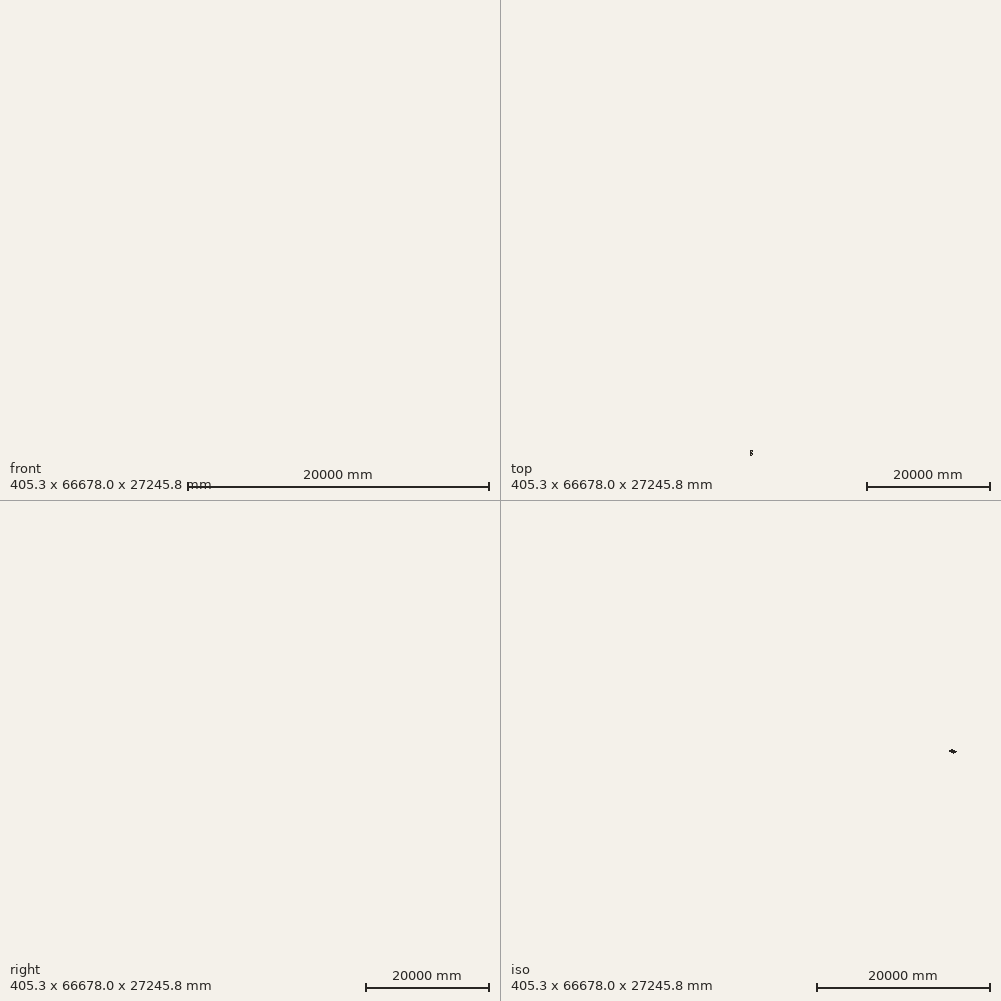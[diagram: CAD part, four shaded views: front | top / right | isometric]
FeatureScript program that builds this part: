
annotation { "Feature Type Name" : "Feature", "Feature Type Description" : "" }
export const myFeature = defineFeature(function(context is Context, id is Id, definition is map)
    precondition{}
    {
        {
            var Q0;
            Q0=qCreatedBy(makeId("Top.planeOp"),FACE);
            var sketch = newSketch(context, id + "F0", { "sketchPlane" : qUnion([Q0])});
            skLineSegment(sketch, "E0", {"start": v(-174.6, -35.65) * mm, "end": v(-124.28, -35.65) * mm});
            skLineSegment(sketch, "E1", {"start": v(-124.28, -35.65) * mm, "end": v(-124.28, -289.85) * mm});
            skLineSegment(sketch, "E2", {"start": v(-124.28, -289.85) * mm, "end": v(-72.03, -289.85) * mm});
            skLineSegment(sketch, "E3", {"start": v(-72.03, -289.85) * mm, "end": v(-72.03, -35.65) * mm});
            skLineSegment(sketch, "E4", {"start": v(-72.03, -35.65) * mm, "end": v(5.25, -35.65) * mm});
            skLineSegment(sketch, "E5", {"start": v(5.25, -35.65) * mm, "end": v(0, -289.85) * mm});
            skLineSegment(sketch, "E6", {"start": v(0, -289.85) * mm, "end": v(50.55, -290.9) * mm});
            skLineSegment(sketch, "E7", {"start": v(50.55, -290.9) * mm, "end": v(50.55, -35.65) * mm});
            skLineSegment(sketch, "E8", {"start": v(50.55, -35.65) * mm, "end": v(126.92, -35.65) * mm});
            skLineSegment(sketch, "E9", {"start": v(126.92, -35.65) * mm, "end": v(126.92, -289.85) * mm});
            skLineSegment(sketch, "E10", {"start": v(126.92, -289.85) * mm, "end": v(179.8, -289.85) * mm});
            skLineSegment(sketch, "E11", {"start": v(179.8, -289.85) * mm, "end": v(179.8, 322.53) * mm});
            skLineSegment(sketch, "E12", {"start": v(179.8, 322.53) * mm, "end": v(126.92, 322.53) * mm});
            skLineSegment(sketch, "E13", {"start": v(126.92, 322.53) * mm, "end": v(126.92, 63.9) * mm});
            skLineSegment(sketch, "E14", {"start": v(126.92, 63.9) * mm, "end": v(50.55, 63.9) * mm});
            skLineSegment(sketch, "E15", {"start": v(50.55, 63.9) * mm, "end": v(50.55, 322.53) * mm});
            skLineSegment(sketch, "E16", {"start": v(50.55, 322.53) * mm, "end": v(5.25, 323.47) * mm});
            skLineSegment(sketch, "E17", {"start": v(5.25, 323.47) * mm, "end": v(5.25, 63.9) * mm});
            skLineSegment(sketch, "E18", {"start": v(5.25, 63.9) * mm, "end": v(-72.03, 65.5) * mm});
            skLineSegment(sketch, "E19", {"start": v(-72.03, 65.5) * mm, "end": v(-72.03, 322.53) * mm});
            skLineSegment(sketch, "E20", {"start": v(-72.03, 322.53) * mm, "end": v(-124.28, 322.53) * mm});
            skLineSegment(sketch, "E21", {"start": v(-124.28, 322.53) * mm, "end": v(-124.28, 63.9) * mm});
            skLineSegment(sketch, "E22", {"start": v(-124.28, 63.9) * mm, "end": v(-174.6, 63.9) * mm});
            skLineSegment(sketch, "E23", {"start": v(-174.6, 63.9) * mm, "end": v(-174.6, 394) * mm});
            skLineSegment(sketch, "E24", {"start": v(-174.6, 394) * mm, "end": v(230.74, 394) * mm});
            skLineSegment(sketch, "E25", {"start": v(230.74, 394) * mm, "end": v(230.74, -369.8) * mm});
            skLineSegment(sketch, "E26", {"start": v(230.74, -369.8) * mm, "end": v(-174.6, -369.8) * mm});
            skLineSegment(sketch, "E27", {"start": v(-174.6, -369.8) * mm, "end": v(-174.6, -35.65) * mm});
            skSolve(sketch);
        }
        {
            var Q0;
            Q0 = qSketchRegion(id + "F0", true);
            extrude(context, id + "F1", {"entities" : qUnion([Q0]), "depth" : 25.4 * mm, "offsetDistance" : 25.4 * mm});
        }
        {
            var Q0;
            Q0=makeQuery(id+"F1.opExtrude","CAP_FACE",FACE,{"disambiguationData":[OSD([sQuery(id+"F0.wireOp",EDGE,"E0"),sQuery(id+"F0.wireOp",EDGE,"E1"),sQuery(id+"F0.wireOp",EDGE,"E2"),sQuery(id+"F0.wireOp",EDGE,"E3"),sQuery(id+"F0.wireOp",EDGE,"E4"),sQuery(id+"F0.wireOp",EDGE,"E5"),sQuery(id+"F0.wireOp",EDGE,"E6"),sQuery(id+"F0.wireOp",EDGE,"E7"),sQuery(id+"F0.wireOp",EDGE,"E8"),sQuery(id+"F0.wireOp",EDGE,"E9"),sQuery(id+"F0.wireOp",EDGE,"E10"),sQuery(id+"F0.wireOp",EDGE,"E11"),sQuery(id+"F0.wireOp",EDGE,"E12"),sQuery(id+"F0.wireOp",EDGE,"E13"),sQuery(id+"F0.wireOp",EDGE,"E14"),sQuery(id+"F0.wireOp",EDGE,"E15"),sQuery(id+"F0.wireOp",EDGE,"E16"),sQuery(id+"F0.wireOp",EDGE,"E17"),sQuery(id+"F0.wireOp",EDGE,"E18"),sQuery(id+"F0.wireOp",EDGE,"E19"),sQuery(id+"F0.wireOp",EDGE,"E20"),sQuery(id+"F0.wireOp",EDGE,"E21"),sQuery(id+"F0.wireOp",EDGE,"E22"),sQuery(id+"F0.wireOp",EDGE,"E23"),sQuery(id+"F0.wireOp",EDGE,"E24"),sQuery(id+"F0.wireOp",EDGE,"E25"),sQuery(id+"F0.wireOp",EDGE,"E26"),sQuery(id+"F0.wireOp",EDGE,"E27")])],"isStart":false});
            shell(context, id + "F2", {"entities" : qUnion([Q0]), "thickness" : 2.54 * mm});
        }
        {
            var Q0;
            Q0=makeQuery(id+"F2.opShell","OFFSET_FACE",FACE,{"disambiguationData":[OSD([sQuery(id+"F0.wireOp",EDGE,"E0"),sQuery(id+"F0.wireOp",EDGE,"E1"),sQuery(id+"F0.wireOp",EDGE,"E2"),sQuery(id+"F0.wireOp",EDGE,"E3"),sQuery(id+"F0.wireOp",EDGE,"E4"),sQuery(id+"F0.wireOp",EDGE,"E5"),sQuery(id+"F0.wireOp",EDGE,"E6"),sQuery(id+"F0.wireOp",EDGE,"E7"),sQuery(id+"F0.wireOp",EDGE,"E8"),sQuery(id+"F0.wireOp",EDGE,"E9"),sQuery(id+"F0.wireOp",EDGE,"E10"),sQuery(id+"F0.wireOp",EDGE,"E11"),sQuery(id+"F0.wireOp",EDGE,"E12"),sQuery(id+"F0.wireOp",EDGE,"E13"),sQuery(id+"F0.wireOp",EDGE,"E14"),sQuery(id+"F0.wireOp",EDGE,"E15"),sQuery(id+"F0.wireOp",EDGE,"E16"),sQuery(id+"F0.wireOp",EDGE,"E17"),sQuery(id+"F0.wireOp",EDGE,"E18"),sQuery(id+"F0.wireOp",EDGE,"E19"),sQuery(id+"F0.wireOp",EDGE,"E20"),sQuery(id+"F0.wireOp",EDGE,"E21"),sQuery(id+"F0.wireOp",EDGE,"E22"),sQuery(id+"F0.wireOp",EDGE,"E23"),sQuery(id+"F0.wireOp",EDGE,"E24"),sQuery(id+"F0.wireOp",EDGE,"E25"),sQuery(id+"F0.wireOp",EDGE,"E26"),sQuery(id+"F0.wireOp",EDGE,"E27")])]});
            var sketch = newSketch(context, id + "F3", { "sketchPlane" : qUnion([Q0])});
            skLineSegment(sketch, "E28.bottom", {"start": v(-172.06, 391.47) * mm, "end": v(-162.53, 391.47) * mm});
            skLineSegment(sketch, "E28.top", {"start": v(-172.06, 381.16) * mm, "end": v(-162.53, 381.16) * mm});
            skLineSegment(sketch, "E28.left", {"start": v(-172.06, 391.47) * mm, "end": v(-172.06, 381.16) * mm});
            skLineSegment(sketch, "E28.right", {"start": v(-162.53, 391.47) * mm, "end": v(-162.53, 381.16) * mm});
            skLineSegment(sketch, "E29.bottom", {"start": v(-172.06, -367.27) * mm, "end": v(-162.53, -367.27) * mm});
            skLineSegment(sketch, "E29.top", {"start": v(-172.06, -358.02) * mm, "end": v(-162.53, -358.02) * mm});
            skLineSegment(sketch, "E29.left", {"start": v(-172.06, -367.27) * mm, "end": v(-172.06, -358.02) * mm});
            skLineSegment(sketch, "E29.right", {"start": v(-162.53, -367.27) * mm, "end": v(-162.53, -358.02) * mm});
            skLineSegment(sketch, "E30.bottom", {"start": v(228.2, -367.27) * mm, "end": v(218.16, -367.27) * mm});
            skLineSegment(sketch, "E30.top", {"start": v(228.2, -358.02) * mm, "end": v(218.16, -358.02) * mm});
            skLineSegment(sketch, "E30.left", {"start": v(228.2, -367.27) * mm, "end": v(228.2, -358.02) * mm});
            skLineSegment(sketch, "E30.right", {"start": v(218.16, -367.27) * mm, "end": v(218.16, -358.02) * mm});
            skSolve(sketch);
        }
        {
            var Q0;
            Q0 = qSketchRegion(id + "F3", true);
            extrude(context, id + "F4", {"entities" : qUnion([Q0]), "operationType" : NewBodyOperationType.ADD, "depth" : 96.52 * mm, "offsetDistance" : 25.4 * mm});
        }
        {
            var Q0;
            Q0=makeQuery(id+"F2.opShell","OFFSET_FACE",FACE,{"disambiguationData":[OSD([sQuery(id+"F0.wireOp",EDGE,"E0"),sQuery(id+"F0.wireOp",EDGE,"E1"),sQuery(id+"F0.wireOp",EDGE,"E2"),sQuery(id+"F0.wireOp",EDGE,"E3"),sQuery(id+"F0.wireOp",EDGE,"E4"),sQuery(id+"F0.wireOp",EDGE,"E5"),sQuery(id+"F0.wireOp",EDGE,"E6"),sQuery(id+"F0.wireOp",EDGE,"E7"),sQuery(id+"F0.wireOp",EDGE,"E8"),sQuery(id+"F0.wireOp",EDGE,"E9"),sQuery(id+"F0.wireOp",EDGE,"E10"),sQuery(id+"F0.wireOp",EDGE,"E11"),sQuery(id+"F0.wireOp",EDGE,"E12"),sQuery(id+"F0.wireOp",EDGE,"E13"),sQuery(id+"F0.wireOp",EDGE,"E14"),sQuery(id+"F0.wireOp",EDGE,"E15"),sQuery(id+"F0.wireOp",EDGE,"E16"),sQuery(id+"F0.wireOp",EDGE,"E17"),sQuery(id+"F0.wireOp",EDGE,"E18"),sQuery(id+"F0.wireOp",EDGE,"E19"),sQuery(id+"F0.wireOp",EDGE,"E20"),sQuery(id+"F0.wireOp",EDGE,"E21"),sQuery(id+"F0.wireOp",EDGE,"E22"),sQuery(id+"F0.wireOp",EDGE,"E23"),sQuery(id+"F0.wireOp",EDGE,"E24"),sQuery(id+"F0.wireOp",EDGE,"E25"),sQuery(id+"F0.wireOp",EDGE,"E26"),sQuery(id+"F0.wireOp",EDGE,"E27")])]});
            var sketch = newSketch(context, id + "F5", { "sketchPlane" : qUnion([Q0])});
            skLineSegment(sketch, "E31.bottom", {"start": v(-172.06, 66.44) * mm, "end": v(-162.53, 66.44) * mm});
            skLineSegment(sketch, "E31.top", {"start": v(-172.06, 76.58) * mm, "end": v(-162.53, 76.58) * mm});
            skLineSegment(sketch, "E31.left", {"start": v(-172.06, 66.44) * mm, "end": v(-172.06, 76.58) * mm});
            skLineSegment(sketch, "E31.right", {"start": v(-162.53, 66.44) * mm, "end": v(-162.53, 76.58) * mm});
            skLineSegment(sketch, "E32.bottom", {"start": v(-172.06, -38.19) * mm, "end": v(-162.53, -38.19) * mm});
            skLineSegment(sketch, "E32.top", {"start": v(-172.06, -47.6) * mm, "end": v(-162.53, -47.6) * mm});
            skLineSegment(sketch, "E32.left", {"start": v(-172.06, -38.19) * mm, "end": v(-172.06, -47.6) * mm});
            skLineSegment(sketch, "E32.right", {"start": v(-162.53, -38.19) * mm, "end": v(-162.53, -47.6) * mm});
            skSolve(sketch);
        }
        {
            var Q0;
            Q0 = qSketchRegion(id + "F5", true);
            extrude(context, id + "F6", {"entities" : qUnion([Q0]), "operationType" : NewBodyOperationType.ADD, "depth" : 193.04 * mm, "offsetDistance" : 25.4 * mm});
        }
        {
            var Q0;
            Q0=qCreatedBy(makeId("Front.planeOp"),FACE);
            var sketch = newSketch(context, id + "F7", { "sketchPlane" : qUnion([Q0])});
            skLineSegment(sketch, "E33.bottom", {"start": v(-172.06, 195.59) * mm, "end": v(-162.5, 195.59) * mm});
            skLineSegment(sketch, "E33.top", {"start": v(-172.06, 204.26) * mm, "end": v(-162.5, 204.26) * mm});
            skLineSegment(sketch, "E33.left", {"start": v(-172.06, 195.59) * mm, "end": v(-172.06, 204.26) * mm});
            skLineSegment(sketch, "E33.right", {"start": v(-162.5, 195.59) * mm, "end": v(-162.5, 204.26) * mm});
            skSolve(sketch);
        }
        {
            var Q0;
            Q0=makeQuery(id+"F1.opExtrude","SWEPT_BODY",BODY,{"disambiguationData":[OSD([sQuery(id+"F0.wireOp",EDGE,"E0"),sQuery(id+"F0.wireOp",EDGE,"E1"),sQuery(id+"F0.wireOp",EDGE,"E2"),sQuery(id+"F0.wireOp",EDGE,"E3"),sQuery(id+"F0.wireOp",EDGE,"E4"),sQuery(id+"F0.wireOp",EDGE,"E5"),sQuery(id+"F0.wireOp",EDGE,"E6"),sQuery(id+"F0.wireOp",EDGE,"E7"),sQuery(id+"F0.wireOp",EDGE,"E8"),sQuery(id+"F0.wireOp",EDGE,"E9"),sQuery(id+"F0.wireOp",EDGE,"E10"),sQuery(id+"F0.wireOp",EDGE,"E11"),sQuery(id+"F0.wireOp",EDGE,"E12"),sQuery(id+"F0.wireOp",EDGE,"E13"),sQuery(id+"F0.wireOp",EDGE,"E14"),sQuery(id+"F0.wireOp",EDGE,"E15"),sQuery(id+"F0.wireOp",EDGE,"E16"),sQuery(id+"F0.wireOp",EDGE,"E17"),sQuery(id+"F0.wireOp",EDGE,"E18"),sQuery(id+"F0.wireOp",EDGE,"E19"),sQuery(id+"F0.wireOp",EDGE,"E20"),sQuery(id+"F0.wireOp",EDGE,"E21"),sQuery(id+"F0.wireOp",EDGE,"E22"),sQuery(id+"F0.wireOp",EDGE,"E23"),sQuery(id+"F0.wireOp",EDGE,"E24"),sQuery(id+"F0.wireOp",EDGE,"E25"),sQuery(id+"F0.wireOp",EDGE,"E26"),sQuery(id+"F0.wireOp",EDGE,"E27")])]});
            var Q1;
            Q1=qCreatedBy(makeId("Front.planeOp"),FACE);
            transform(context, id + "F8", {"entities" : qUnion([Q0]), "transformType" : TransformType.TRANSLATION_DISTANCE, "transformDirection" : qUnion([Q1]), "distance" : 13.72 * mm, "makeCopy" : false});
        }
        {
            var Q0;
            Q0=makeQuery(id+"F7.imprint","IMPRINT",FACE,{"disambiguationData":[TD([[makeQuery(id+"F7.imprint","IMPRINT",EDGE,{"derivedFrom":sQuery(id+"F7.wireOp",EDGE,"E33.bottom")}),1.0]])]});
            extrude(context, id + "F9", {"entities" : qUnion([Q0]), "endBound" : BoundingType.SYMMETRIC, "depth" : 170.7 * mm, "offsetDistance" : 25.4 * mm});
        }
        {
            var Q0;
            Q0=makeQuery(id+"F9.opExtrude","CAP_EDGE",EDGE,{"disambiguationData":[OSD([sQuery(id+"F7.wireOp",EDGE,"E33.bottom")])],"isStart":true});
            var Q1;
            Q1=makeQuery(id+"F9.opExtrude","CAP_EDGE",EDGE,{"disambiguationData":[OSD([sQuery(id+"F7.wireOp",EDGE,"E33.bottom")])],"isStart":false});
            chamfer(context, id + "F10", {"entities" : qUnion([Q0, Q1]), "width" : 5.08 * mm, "tangentPropagation" : true});
        }
        {
            var Q0;
            Q0=makeQuery(id+"F2.opShell","OFFSET_FACE",FACE,{"disambiguationData":[OSD([sQuery(id+"F0.wireOp",EDGE,"E0"),sQuery(id+"F0.wireOp",EDGE,"E1"),sQuery(id+"F0.wireOp",EDGE,"E2"),sQuery(id+"F0.wireOp",EDGE,"E3"),sQuery(id+"F0.wireOp",EDGE,"E4"),sQuery(id+"F0.wireOp",EDGE,"E5"),sQuery(id+"F0.wireOp",EDGE,"E6"),sQuery(id+"F0.wireOp",EDGE,"E7"),sQuery(id+"F0.wireOp",EDGE,"E8"),sQuery(id+"F0.wireOp",EDGE,"E9"),sQuery(id+"F0.wireOp",EDGE,"E10"),sQuery(id+"F0.wireOp",EDGE,"E11"),sQuery(id+"F0.wireOp",EDGE,"E12"),sQuery(id+"F0.wireOp",EDGE,"E13"),sQuery(id+"F0.wireOp",EDGE,"E14"),sQuery(id+"F0.wireOp",EDGE,"E15"),sQuery(id+"F0.wireOp",EDGE,"E16"),sQuery(id+"F0.wireOp",EDGE,"E17"),sQuery(id+"F0.wireOp",EDGE,"E18"),sQuery(id+"F0.wireOp",EDGE,"E19"),sQuery(id+"F0.wireOp",EDGE,"E20"),sQuery(id+"F0.wireOp",EDGE,"E21"),sQuery(id+"F0.wireOp",EDGE,"E22"),sQuery(id+"F0.wireOp",EDGE,"E23"),sQuery(id+"F0.wireOp",EDGE,"E24"),sQuery(id+"F0.wireOp",EDGE,"E25"),sQuery(id+"F0.wireOp",EDGE,"E26"),sQuery(id+"F0.wireOp",EDGE,"E27")])]});
            var sketch = newSketch(context, id + "F11", { "sketchPlane" : qUnion([Q0])});
            skLineSegment(sketch, "E34.bottom", {"start": v(228.2, 377.75) * mm, "end": v(218.12, 377.75) * mm});
            skLineSegment(sketch, "E34.top", {"start": v(228.2, 367.35) * mm, "end": v(218.12, 367.35) * mm});
            skLineSegment(sketch, "E34.left", {"start": v(228.2, 377.75) * mm, "end": v(228.2, 367.35) * mm});
            skLineSegment(sketch, "E34.right", {"start": v(218.12, 377.75) * mm, "end": v(218.12, 367.35) * mm});
            skSolve(sketch);
        }
        {
            var Q0;
            Q0 = qSketchRegion(id + "F11", true);
            extrude(context, id + "F12", {"entities" : qUnion([Q0]), "operationType" : NewBodyOperationType.ADD, "depth" : 22.86 * mm, "offsetDistance" : 25.4 * mm});
        }
        {
            var Q0;
            Q0=makeQuery(id+"F4.opExtrude","SWEPT_FACE",FACE,{"disambiguationData":[OSD([sQuery(id+"F3.wireOp",EDGE,"E29.left")])]});
            var sketch = newSketch(context, id + "F13", { "sketchPlane" : qUnion([Q0])});
            skLineSegment(sketch, "E35.bottom", {"start": v(380.99, 99.06) * mm, "end": v(382.68, 99.06) * mm});
            skLineSegment(sketch, "E35.top", {"start": v(380.99, 91.4) * mm, "end": v(382.68, 91.4) * mm});
            skLineSegment(sketch, "E35.left", {"start": v(380.99, 99.06) * mm, "end": v(380.99, 91.4) * mm});
            skLineSegment(sketch, "E35.right", {"start": v(382.68, 99.06) * mm, "end": v(382.68, 91.4) * mm});
            skSolve(sketch);
        }
        {
            var Q0;
            Q0 = qSketchRegion(id + "F13", true);
            extrude(context, id + "F14", {"entities" : qUnion([Q0]), "operationType" : NewBodyOperationType.ADD, "oppositeDirection" : true, "depth" : 401.83 * mm, "offsetDistance" : 25.4 * mm});
        }
        {
            var Q0;
            Q0=makeQuery(id+"F14.opExtrude","SWEPT_FACE",FACE,{"disambiguationData":[OSD([sQuery(id+"F13.wireOp",EDGE,"E35.right")])]});
            var sketch = newSketch(context, id + "F15", { "sketchPlane" : qUnion([Q0])});
            skLineSegment(sketch, "E36.bottom", {"start": v(-172.06, 99.06) * mm, "end": v(-173.53, 99.06) * mm});
            skLineSegment(sketch, "E36.top", {"start": v(-172.06, 91.4) * mm, "end": v(-173.53, 91.4) * mm});
            skLineSegment(sketch, "E36.left", {"start": v(-172.06, 99.06) * mm, "end": v(-172.06, 91.4) * mm});
            skLineSegment(sketch, "E36.right", {"start": v(-173.53, 99.06) * mm, "end": v(-173.53, 91.4) * mm});
            skSolve(sketch);
        }
        {
            var Q0;
            Q0 = qSketchRegion(id + "F15", true);
            extrude(context, id + "F16", {"entities" : qUnion([Q0]), "operationType" : NewBodyOperationType.ADD, "oppositeDirection" : true, "depth" : 330.76 * mm, "offsetDistance" : 25.4 * mm});
        }
        {
            var Q0;
            Q0=makeQuery(id+"F6.opExtrude","SWEPT_FACE",FACE,{"disambiguationData":[OSD([sQuery(id+"F5.wireOp",EDGE,"E31.bottom")])]});
            var sketch = newSketch(context, id + "F17", { "sketchPlane" : qUnion([Q0])});
            skLineSegment(sketch, "E37.bottom", {"start": v(-172.06, 99.07) * mm, "end": v(-173.62, 99.07) * mm});
            skLineSegment(sketch, "E37.top", {"start": v(-172.06, 91.41) * mm, "end": v(-173.62, 91.41) * mm});
            skLineSegment(sketch, "E37.left", {"start": v(-172.06, 99.07) * mm, "end": v(-172.06, 91.41) * mm});
            skLineSegment(sketch, "E37.right", {"start": v(-173.62, 99.07) * mm, "end": v(-173.62, 91.41) * mm});
            skSolve(sketch);
        }
        {
            var Q0;
            Q0 = qSketchRegion(id + "F17", true);
            extrude(context, id + "F18", {"entities" : qUnion([Q0]), "operationType" : NewBodyOperationType.ADD, "oppositeDirection" : true, "depth" : 324.87 * mm, "offsetDistance" : 25.4 * mm});
        }
        {
            var Q0;
            Q0=makeQuery(id+"F2.opShell","OFFSET_FACE",FACE,{"disambiguationData":[OSD([sQuery(id+"F0.wireOp",EDGE,"E0"),sQuery(id+"F0.wireOp",EDGE,"E1"),sQuery(id+"F0.wireOp",EDGE,"E2"),sQuery(id+"F0.wireOp",EDGE,"E3"),sQuery(id+"F0.wireOp",EDGE,"E4"),sQuery(id+"F0.wireOp",EDGE,"E5"),sQuery(id+"F0.wireOp",EDGE,"E6"),sQuery(id+"F0.wireOp",EDGE,"E7"),sQuery(id+"F0.wireOp",EDGE,"E8"),sQuery(id+"F0.wireOp",EDGE,"E9"),sQuery(id+"F0.wireOp",EDGE,"E10"),sQuery(id+"F0.wireOp",EDGE,"E11"),sQuery(id+"F0.wireOp",EDGE,"E12"),sQuery(id+"F0.wireOp",EDGE,"E13"),sQuery(id+"F0.wireOp",EDGE,"E14"),sQuery(id+"F0.wireOp",EDGE,"E15"),sQuery(id+"F0.wireOp",EDGE,"E16"),sQuery(id+"F0.wireOp",EDGE,"E17"),sQuery(id+"F0.wireOp",EDGE,"E18"),sQuery(id+"F0.wireOp",EDGE,"E19"),sQuery(id+"F0.wireOp",EDGE,"E20"),sQuery(id+"F0.wireOp",EDGE,"E21"),sQuery(id+"F0.wireOp",EDGE,"E22"),sQuery(id+"F0.wireOp",EDGE,"E23"),sQuery(id+"F0.wireOp",EDGE,"E24"),sQuery(id+"F0.wireOp",EDGE,"E25"),sQuery(id+"F0.wireOp",EDGE,"E26"),sQuery(id+"F0.wireOp",EDGE,"E27")])]});
            var sketch = newSketch(context, id + "F19", { "sketchPlane" : qUnion([Q0])});
            skLineSegment(sketch, "E38.bottom", {"start": v(-172.06, 215.16) * mm, "end": v(-162.53, 215.16) * mm});
            skLineSegment(sketch, "E38.top", {"start": v(-172.06, 224.54) * mm, "end": v(-162.53, 224.54) * mm});
            skLineSegment(sketch, "E38.left", {"start": v(-172.06, 215.16) * mm, "end": v(-172.06, 224.54) * mm});
            skLineSegment(sketch, "E38.right", {"start": v(-162.53, 215.16) * mm, "end": v(-162.53, 224.54) * mm});
            skLineSegment(sketch, "E39.bottom", {"start": v(-172.06, -216.52) * mm, "end": v(-162.53, -216.52) * mm});
            skLineSegment(sketch, "E39.top", {"start": v(-172.06, -226) * mm, "end": v(-162.53, -226) * mm});
            skLineSegment(sketch, "E39.left", {"start": v(-172.06, -216.52) * mm, "end": v(-172.06, -226) * mm});
            skLineSegment(sketch, "E39.right", {"start": v(-162.53, -216.52) * mm, "end": v(-162.53, -226) * mm});
            skLineSegment(sketch, "E40.bottom", {"start": v(27.81, -380.99) * mm, "end": v(36.97, -380.99) * mm});
            skLineSegment(sketch, "E40.top", {"start": v(27.81, -371.74) * mm, "end": v(36.97, -371.74) * mm});
            skLineSegment(sketch, "E40.left", {"start": v(27.81, -380.99) * mm, "end": v(27.81, -371.74) * mm});
            skLineSegment(sketch, "E40.right", {"start": v(36.97, -380.99) * mm, "end": v(36.97, -371.74) * mm});
            skSolve(sketch);
        }
        {
            var Q0;
            Q0 = qSketchRegion(id + "F19", true);
            extrude(context, id + "F20", {"entities" : qUnion([Q0]), "operationType" : NewBodyOperationType.ADD, "depth" : 96.52 * mm, "offsetDistance" : 25.4 * mm});
        }
        {
            var Q0;
            {var subQ0=sQuery(id+"F17.wireOp",EDGE,"E37.bottom");var subQ2=sQuery(id+"F5.wireOp",EDGE,"E31.left");Q0=makeQuery(id+"F18.boolean.opBoolean","SPLIT",FACE,{"disambiguationData":[TD([makeQuery(id+"F18.opExtrude","SWEPT_FACE",FACE,{"disambiguationData":[OSD([subQ0])]})])],"derivedFrom":makeQuery(id+"F6.opExtrude","SWEPT_FACE",FACE,{"disambiguationData":[OSD([subQ2])]})});}
            var sketch = newSketch(context, id + "F21", { "sketchPlane" : qUnion([Q0])});
            skLineSegment(sketch, "E41.bottom", {"start": v(-52.73, 195.58) * mm, "end": v(51.02, 195.58) * mm});
            skLineSegment(sketch, "E41.top", {"start": v(-52.73, 0) * mm, "end": v(51.02, 0) * mm});
            skLineSegment(sketch, "E41.left", {"start": v(-52.73, 195.58) * mm, "end": v(-52.73, 0) * mm});
            skLineSegment(sketch, "E41.right", {"start": v(51.02, 195.58) * mm, "end": v(51.02, 0) * mm});
            skSolve(sketch);
        }
        {
            var Q0;
            Q0 = qSketchRegion(id + "F21", true);
            extrude(context, id + "F22", {"entities" : qUnion([Q0]), "oppositeDirection" : true, "depth" : 5.33 * mm, "offsetDistance" : 25.4 * mm});
        }
        {
            var Q0;
            Q0=makeQuery(id+"F22.opExtrude","CAP_FACE",FACE,{"disambiguationData":[OSD([sQuery(id+"F21.wireOp",EDGE,"E41.bottom"),sQuery(id+"F21.wireOp",EDGE,"E41.top"),sQuery(id+"F21.wireOp",EDGE,"E41.left"),sQuery(id+"F21.wireOp",EDGE,"E41.right")])],"isStart":true});
            var sketch = newSketch(context, id + "F23", { "sketchPlane" : qUnion([Q0])});
            skLineSegment(sketch, "E42.bottom", {"start": v(-46.42, 190.05) * mm, "end": v(43.98, 190.05) * mm});
            skLineSegment(sketch, "E42.top", {"start": v(-46.42, 79.04) * mm, "end": v(43.98, 79.04) * mm});
            skLineSegment(sketch, "E42.left", {"start": v(-46.42, 190.05) * mm, "end": v(-46.42, 79.04) * mm});
            skLineSegment(sketch, "E42.right", {"start": v(43.98, 190.05) * mm, "end": v(43.98, 79.04) * mm});
            skSolve(sketch);
        }
        {
            var Q0;
            Q0 = qSketchRegion(id + "F23", true);
            extrude(context, id + "F24", {"entities" : qUnion([Q0]), "operationType" : NewBodyOperationType.REMOVE, "oppositeDirection" : true, "depth" : 7.37 * mm, "offsetDistance" : 25.4 * mm});
        }
        {
            var Q0;
            Q0=makeQuery(id+"F22.opExtrude","CAP_FACE",FACE,{"disambiguationData":[OSD([sQuery(id+"F21.wireOp",EDGE,"E41.bottom"),sQuery(id+"F21.wireOp",EDGE,"E41.top"),sQuery(id+"F21.wireOp",EDGE,"E41.left"),sQuery(id+"F21.wireOp",EDGE,"E41.right")])],"isStart":true});
            var sketch = newSketch(context, id + "F25", { "sketchPlane" : qUnion([Q0])});
            skLineSegment(sketch, "E43.bottom", {"start": v(-7.07, 68.72) * mm, "end": v(-44.7, 68.72) * mm});
            skLineSegment(sketch, "E43.top", {"start": v(-7.07, 19.41) * mm, "end": v(-44.7, 19.41) * mm});
            skLineSegment(sketch, "E43.left", {"start": v(-7.07, 68.72) * mm, "end": v(-7.07, 19.41) * mm});
            skLineSegment(sketch, "E43.right", {"start": v(-44.7, 68.72) * mm, "end": v(-44.7, 19.41) * mm});
            skLineSegment(sketch, "E44.bottom", {"start": v(6.23, 69.05) * mm, "end": v(43.54, 69.05) * mm});
            skLineSegment(sketch, "E44.top", {"start": v(6.23, 19.41) * mm, "end": v(43.54, 19.41) * mm});
            skLineSegment(sketch, "E44.left", {"start": v(6.23, 69.05) * mm, "end": v(6.23, 19.41) * mm});
            skLineSegment(sketch, "E44.right", {"start": v(43.54, 69.05) * mm, "end": v(43.54, 19.41) * mm});
            skSolve(sketch);
        }
        {
            var Q0;
            Q0 = qSketchRegion(id + "F25", true);
            extrude(context, id + "F26", {"entities" : qUnion([Q0]), "operationType" : NewBodyOperationType.REMOVE, "oppositeDirection" : true, "depth" : 5.08 * mm, "offsetDistance" : 25.4 * mm});
        }
        {
            var Q0;
            Q0=makeQuery(id+"F1.opExtrude","SWEPT_FACE",FACE,{"disambiguationData":[OSD([sQuery(id+"F0.wireOp",EDGE,"E18")])]});
            var sketch = newSketch(context, id + "F27", { "sketchPlane" : qUnion([Q0])});
            skArc(sketch, "E45", {"start": v(4.21, 25.4) * mm, "mid": v(-34.44, 64.05) * mm, "end": v(-73.09, 25.4) * mm});
            skSolve(sketch);
        }
        {
            var Q0;
            Q0 = qSketchRegion(id + "F27", true);
            var Q1;
            Q1=sQuery(id+"F27.wireOp",EDGE,"E45");
            extrude(context, id + "F28", {"entities" : qUnion([Q0]), "bodyType" : ToolBodyType.SURFACE, "operationType" : NewBodyOperationType.ADD, "surfaceEntities" : qUnion([Q1]), "oppositeDirection" : true, "depth" : 260.1 * mm, "offsetDistance" : 25.4 * mm});
        }
        {
            var Q0;
            Q0=makeQuery(id+"F27.imprint","IMPRINT",FACE,{"disambiguationData":[TD([[makeQuery(id+"F27.imprint","IMPRINT",EDGE,{"derivedFrom":sQuery(id+"F27.wireOp",EDGE,"E45")}),1.0]])]});
            var sketch = newSketch(context, id + "F29", { "sketchPlane" : qUnion([Q0])});
            skCircle(sketch, "E46", {"center": v(-34.24, 25.94) * mm, "radius": 2.03 * mm});
            skSolve(sketch);
        }
        {
            var Q0;
            Q0 = qSketchRegion(id + "F29", true);
            extrude(context, id + "F30", {"entities" : qUnion([Q0]), "operationType" : NewBodyOperationType.ADD, "oppositeDirection" : true, "depth" : 291.6 * mm, "offsetDistance" : 25.4 * mm});
        }
        {
            var Q0;
            {var subQ4=sQuery(id+"F0.wireOp",EDGE,"E23");Q0=makeQuery(id+"F20.boolean.opBoolean","SPLIT",FACE,{"disambiguationData":[TD([makeQuery(id+"F4.opExtrude","SWEPT_FACE",FACE,{"disambiguationData":[OSD([sQuery(id+"F3.wireOp",EDGE,"E28.top")])]})])],"derivedFrom":makeQuery(id+"F2.opShell","OFFSET_FACE",FACE,{"disambiguationData":[OSD([subQ4])]})});}
            var sketch = newSketch(context, id + "F31", { "sketchPlane" : qUnion([Q0])});
            skCircle(sketch, "E47", {"center": v(343.04, 25.4) * mm, "radius": 3.46 * mm});
            skCircle(sketch, "E48", {"center": v(66291.03, -27038.09) * mm, "radius": 3.46 * mm});
            skSolve(sketch);
        }
        {
            var Q0;
            Q0 = qSketchRegion(id + "F31", true);
            extrude(context, id + "F32", {"entities" : qUnion([Q0]), "operationType" : NewBodyOperationType.ADD, "depth" : 380.5 * mm, "offsetDistance" : 25.4 * mm});
        }
        {
            var Q0;
            Q0=makeQuery(id+"F2.opShell","OFFSET_FACE",FACE,{"disambiguationData":[OSD([sQuery(id+"F0.wireOp",EDGE,"E14")])]});
            var sketch = newSketch(context, id + "F33", { "sketchPlane" : qUnion([Q0])});
            skCircle(sketch, "E49", {"center": v(-88.73, 25.4) * mm, "radius": 1.83 * mm});
            skSolve(sketch);
        }
        {
            var Q0;
            Q0 = qSketchRegion(id + "F33", true);
            extrude(context, id + "F34", {"entities" : qUnion([Q0]), "operationType" : NewBodyOperationType.ADD, "depth" : 290.32 * mm, "offsetDistance" : 25.4 * mm});
        }
    });
